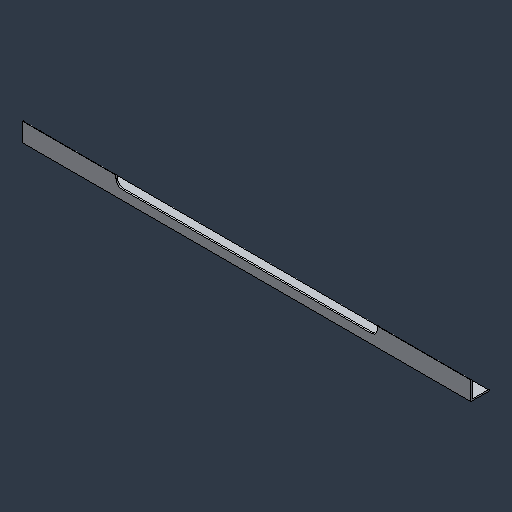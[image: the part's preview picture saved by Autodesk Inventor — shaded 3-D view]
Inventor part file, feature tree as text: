
AUTODESK INVENTOR PART (.ipt)
format: ipt  version: 2024.3 (Build 283343000, 343)  size: 86,016 bytes
history: native  units: mm (DEFAULTED — no unit token found)
features: fillet x1
ambient origin geometry x8: Origin, YZ Plane, XZ Plane, XY Plane, X Axis, Y Axis, Z Axis, Center Point
bodies: Solid1 (feature_tree)
feature tree (1):
  fillet  "Fillet1"  [1 undecoded]
note: 1 required parameter value undecoded (feature->parameter linkage not recoverable at this tier; creation-order binding heuristic only, values carry confidence <= 0.55)
